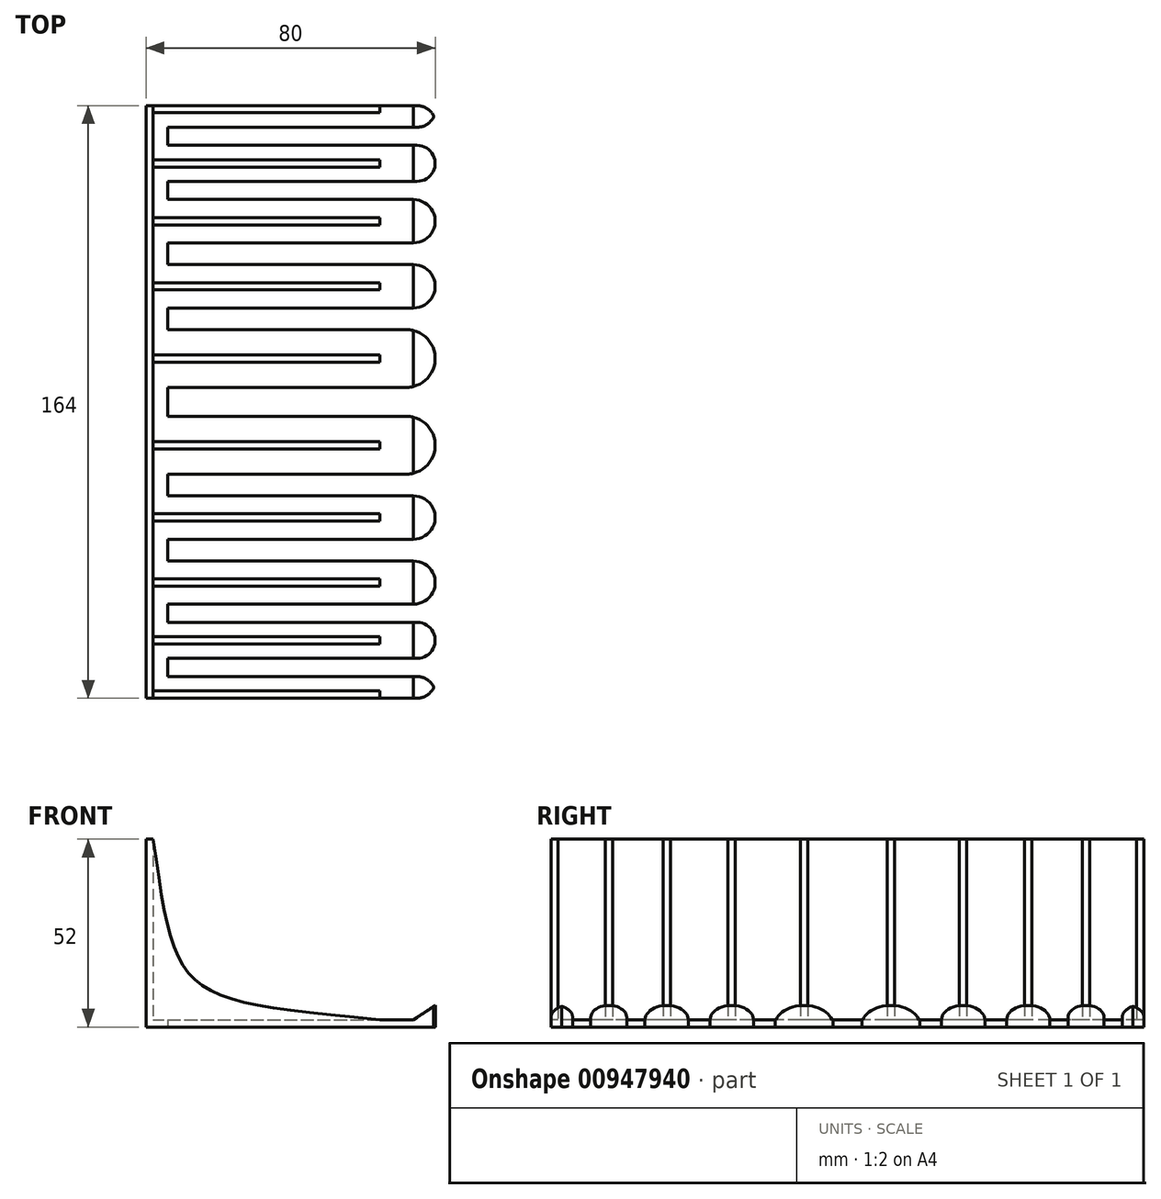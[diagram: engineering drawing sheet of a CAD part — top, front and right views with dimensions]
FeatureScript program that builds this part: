
annotation { "Feature Type Name" : "Feature", "Feature Type Description" : "" }
export const myFeature = defineFeature(function(context is Context, id is Id, definition is map)
    precondition{}
    {
        {
            assignVariable(context, id + "F0", {"name" : "thickness", "anyValue" : 2});
        }
        {
            assignVariable(context, id + "F1", {"name" : "height", "anyValue" : 50});
        }
        {
            var Q0;
            Q0=qCreatedBy(makeId("Top.planeOp"),FACE);
            var sketch = newSketch(context, id + "F2", { "sketchPlane" : qUnion([Q0])});
            skLineSegment(sketch, "E0", {"start": v(-21.89, -82.1) * mm, "end": v(47.11, -82.1) * mm});
            skLineSegment(sketch, "E1", {"start": v(52.11, -77.1) * mm, "end": v(52.11, -77.1) * mm});
            skLineSegment(sketch, "E2", {"start": v(47.11, -72.1) * mm, "end": v(-21.89, -72.1) * mm});
            skLineSegment(sketch, "E3", {"start": v(-21.89, -72.1) * mm, "end": v(-21.89, -67.1) * mm});
            skLineSegment(sketch, "E4", {"start": v(-21.89, -67.1) * mm, "end": v(46.11, -67.1) * mm});
            skLineSegment(sketch, "E5", {"start": v(52.11, -61.1) * mm, "end": v(52.11, -61.1) * mm});
            skLineSegment(sketch, "E6", {"start": v(46.11, -55.1) * mm, "end": v(-21.89, -55.1) * mm});
            skLineSegment(sketch, "E7", {"start": v(-21.89, -55.1) * mm, "end": v(-21.89, -49.1) * mm});
            skLineSegment(sketch, "E8", {"start": v(-21.89, -49.1) * mm, "end": v(46.11, -49.1) * mm});
            skLineSegment(sketch, "E9", {"start": v(52.11, -43.1) * mm, "end": v(52.11, -43.1) * mm});
            skLineSegment(sketch, "E10", {"start": v(46.11, -37.1) * mm, "end": v(-21.89, -37.1) * mm});
            skLineSegment(sketch, "E11", {"start": v(-21.89, -37.1) * mm, "end": v(-21.89, -31.1) * mm});
            skLineSegment(sketch, "E12", {"start": v(-21.89, -31.1) * mm, "end": v(44.11, -31.1) * mm});
            skLineSegment(sketch, "E13", {"start": v(52.11, -23.1) * mm, "end": v(52.11, -23.1) * mm});
            skLineSegment(sketch, "E14", {"start": v(44.11, -15.1) * mm, "end": v(-21.89, -15.1) * mm});
            skLineSegment(sketch, "E15", {"start": v(-21.89, -15.1) * mm, "end": v(-21.89, -7.1) * mm});
            skLineSegment(sketch, "E16", {"start": v(-21.89, -7.1) * mm, "end": v(44.11, -7.1) * mm});
            skLineSegment(sketch, "E17", {"start": v(52.11, 0.9) * mm, "end": v(52.11, 0.9) * mm});
            skLineSegment(sketch, "E18", {"start": v(44.11, 8.9) * mm, "end": v(-21.89, 8.9) * mm});
            skLineSegment(sketch, "E19", {"start": v(-21.89, 8.9) * mm, "end": v(-21.89, 14.9) * mm});
            skLineSegment(sketch, "E20", {"start": v(-21.89, 14.9) * mm, "end": v(46.11, 14.9) * mm});
            skLineSegment(sketch, "E21", {"start": v(52.11, 20.9) * mm, "end": v(52.11, 20.9) * mm});
            skLineSegment(sketch, "E22", {"start": v(46.11, 26.9) * mm, "end": v(-21.89, 26.9) * mm});
            skLineSegment(sketch, "E23", {"start": v(-21.89, 26.9) * mm, "end": v(-21.89, 32.9) * mm});
            skLineSegment(sketch, "E24", {"start": v(-21.89, 32.9) * mm, "end": v(46.11, 32.9) * mm});
            skLineSegment(sketch, "E25", {"start": v(52.11, 38.9) * mm, "end": v(52.11, 38.9) * mm});
            skLineSegment(sketch, "E26", {"start": v(46.11, 44.9) * mm, "end": v(-21.89, 44.9) * mm});
            skLineSegment(sketch, "E27", {"start": v(-21.89, 44.9) * mm, "end": v(-21.89, 49.9) * mm});
            skLineSegment(sketch, "E28", {"start": v(-21.89, 49.9) * mm, "end": v(47.11, 49.9) * mm});
            skLineSegment(sketch, "E29", {"start": v(52.11, 54.9) * mm, "end": v(52.11, 54.9) * mm});
            skLineSegment(sketch, "E30", {"start": v(47.11, 59.9) * mm, "end": v(-21.89, 59.9) * mm});
            skLineSegment(sketch, "E31", {"start": v(-21.89, -82.1) * mm, "end": v(-21.89, -87.1) * mm});
            skLineSegment(sketch, "E32", {"start": v(-21.89, -87.1) * mm, "end": v(47.11, -87.1) * mm});
            skLineSegment(sketch, "E33", {"start": v(52.11, -88.1) * mm, "end": v(52.11, -92.1) * mm});
            skLineSegment(sketch, "E34", {"start": v(47.11, -93.1) * mm, "end": v(-27.89, -93.1) * mm});
            skLineSegment(sketch, "E35", {"start": v(-21.89, 59.9) * mm, "end": v(-21.89, 64.9) * mm});
            skLineSegment(sketch, "E36", {"start": v(-21.89, 64.9) * mm, "end": v(47.11, 64.9) * mm});
            skLineSegment(sketch, "E37", {"start": v(52.11, 65.9) * mm, "end": v(52.11, 69.9) * mm});
            skLineSegment(sketch, "E38", {"start": v(47.11, 70.9) * mm, "end": v(-27.89, 70.9) * mm});
            skLineSegment(sketch, "E39", {"start": v(-27.89, 70.9) * mm, "end": v(-27.89, -93.1) * mm});
            skPoint(sketch, "E40.visualSharp", {"position": v(52.11, 70.9) * mm});
            skArc(sketch, "E40.filletArc", {"start": v(52.11, 65.9) * mm, "mid": v(50.65, 69.43) * mm, "end": v(47.11, 70.9) * mm});
            skPoint(sketch, "E41.visualSharp", {"position": v(52.11, 64.9) * mm});
            skArc(sketch, "E41.filletArc", {"start": v(47.11, 64.9) * mm, "mid": v(50.65, 66.36) * mm, "end": v(52.11, 69.9) * mm});
            skPoint(sketch, "E42.visualSharp", {"position": v(52.11, 59.9) * mm});
            skArc(sketch, "E42.filletArc", {"start": v(52.11, 54.9) * mm, "mid": v(50.65, 58.43) * mm, "end": v(47.11, 59.9) * mm});
            skPoint(sketch, "E43.visualSharp", {"position": v(52.11, 49.9) * mm});
            skArc(sketch, "E43.filletArc", {"start": v(47.11, 49.9) * mm, "mid": v(50.65, 51.36) * mm, "end": v(52.11, 54.9) * mm});
            skPoint(sketch, "E44.visualSharp", {"position": v(52.11, -87.1) * mm});
            skArc(sketch, "E44.filletArc", {"start": v(52.11, -92.1) * mm, "mid": v(50.65, -88.57) * mm, "end": v(47.11, -87.1) * mm});
            skPoint(sketch, "E45.visualSharp", {"position": v(52.11, -93.1) * mm});
            skArc(sketch, "E45.filletArc", {"start": v(47.11, -93.1) * mm, "mid": v(50.65, -91.64) * mm, "end": v(52.11, -88.1) * mm});
            skPoint(sketch, "E46.visualSharp", {"position": v(52.11, -82.1) * mm});
            skArc(sketch, "E46.filletArc", {"start": v(47.11, -82.1) * mm, "mid": v(50.65, -80.64) * mm, "end": v(52.11, -77.1) * mm});
            skPoint(sketch, "E47.visualSharp", {"position": v(52.11, -72.1) * mm});
            skArc(sketch, "E47.filletArc", {"start": v(52.11, -77.1) * mm, "mid": v(50.65, -73.57) * mm, "end": v(47.11, -72.1) * mm});
            skPoint(sketch, "E48.visualSharp", {"position": v(52.11, -67.1) * mm});
            skArc(sketch, "E48.filletArc", {"start": v(46.11, -67.1) * mm, "mid": v(50.35, -65.35) * mm, "end": v(52.11, -61.1) * mm});
            skPoint(sketch, "E49.visualSharp", {"position": v(52.11, -55.1) * mm});
            skArc(sketch, "E49.filletArc", {"start": v(52.11, -61.1) * mm, "mid": v(50.35, -56.86) * mm, "end": v(46.11, -55.1) * mm});
            skPoint(sketch, "E50.visualSharp", {"position": v(52.11, -49.1) * mm});
            skArc(sketch, "E50.filletArc", {"start": v(46.11, -49.1) * mm, "mid": v(50.35, -47.35) * mm, "end": v(52.11, -43.1) * mm});
            skPoint(sketch, "E51.visualSharp", {"position": v(52.11, -37.1) * mm});
            skArc(sketch, "E51.filletArc", {"start": v(52.11, -43.1) * mm, "mid": v(50.35, -38.86) * mm, "end": v(46.11, -37.1) * mm});
            skPoint(sketch, "E52.visualSharp", {"position": v(52.11, 44.9) * mm});
            skArc(sketch, "E52.filletArc", {"start": v(52.11, 38.9) * mm, "mid": v(50.35, 43.14) * mm, "end": v(46.11, 44.9) * mm});
            skPoint(sketch, "E53.visualSharp", {"position": v(52.11, 32.9) * mm});
            skArc(sketch, "E53.filletArc", {"start": v(46.11, 32.9) * mm, "mid": v(50.35, 34.65) * mm, "end": v(52.11, 38.9) * mm});
            skPoint(sketch, "E54.visualSharp", {"position": v(52.11, 26.9) * mm});
            skArc(sketch, "E54.filletArc", {"start": v(52.11, 20.9) * mm, "mid": v(50.35, 25.14) * mm, "end": v(46.11, 26.9) * mm});
            skPoint(sketch, "E55.visualSharp", {"position": v(52.11, 14.9) * mm});
            skArc(sketch, "E55.filletArc", {"start": v(46.11, 14.9) * mm, "mid": v(50.35, 16.65) * mm, "end": v(52.11, 20.9) * mm});
            skPoint(sketch, "E56.visualSharp", {"position": v(52.11, 8.9) * mm});
            skArc(sketch, "E56.filletArc", {"start": v(52.11, 0.9) * mm, "mid": v(49.77, 6.55) * mm, "end": v(44.11, 8.9) * mm});
            skPoint(sketch, "E57.visualSharp", {"position": v(52.11, -7.1) * mm});
            skArc(sketch, "E57.filletArc", {"start": v(44.11, -7.1) * mm, "mid": v(49.77, -4.76) * mm, "end": v(52.11, 0.9) * mm});
            skPoint(sketch, "E58.visualSharp", {"position": v(52.11, -15.1) * mm});
            skArc(sketch, "E58.filletArc", {"start": v(52.11, -23.1) * mm, "mid": v(49.77, -17.45) * mm, "end": v(44.11, -15.1) * mm});
            skPoint(sketch, "E59.visualSharp", {"position": v(52.11, -31.1) * mm});
            skArc(sketch, "E59.filletArc", {"start": v(44.11, -31.1) * mm, "mid": v(49.77, -28.76) * mm, "end": v(52.11, -23.1) * mm});
            skSolve(sketch);
        }
        {
            var Q0;
            Q0=makeQuery(id+"F2.imprint","IMPRINT",FACE,{"disambiguationData":[TD([[makeQuery(id+"F2.imprint","IMPRINT",EDGE,{"derivedFrom":sQuery(id+"F2.wireOp",EDGE,"E0")}),1.0]])]});
            extrude(context, id + "F3", {"entities" : qUnion([Q0]), "depth" : getVariable(context, 'thickness') * mm, "offsetDistance" : 25 * mm});
        }
        {
            var Q0;
            Q0=makeQuery(id+"F3.opExtrude","CAP_FACE",FACE,{"disambiguationData":[OSD([sQuery(id+"F2.wireOp",EDGE,"E0"),sQuery(id+"F2.wireOp",EDGE,"E2"),sQuery(id+"F2.wireOp",EDGE,"E3"),sQuery(id+"F2.wireOp",EDGE,"E4"),sQuery(id+"F2.wireOp",EDGE,"E6"),sQuery(id+"F2.wireOp",EDGE,"E7"),sQuery(id+"F2.wireOp",EDGE,"E8"),sQuery(id+"F2.wireOp",EDGE,"E10"),sQuery(id+"F2.wireOp",EDGE,"E11"),sQuery(id+"F2.wireOp",EDGE,"E12"),sQuery(id+"F2.wireOp",EDGE,"E14"),sQuery(id+"F2.wireOp",EDGE,"E15"),sQuery(id+"F2.wireOp",EDGE,"E16"),sQuery(id+"F2.wireOp",EDGE,"E18"),sQuery(id+"F2.wireOp",EDGE,"E19"),sQuery(id+"F2.wireOp",EDGE,"E20"),sQuery(id+"F2.wireOp",EDGE,"E22"),sQuery(id+"F2.wireOp",EDGE,"E23"),sQuery(id+"F2.wireOp",EDGE,"E24"),sQuery(id+"F2.wireOp",EDGE,"E26"),sQuery(id+"F2.wireOp",EDGE,"E27"),sQuery(id+"F2.wireOp",EDGE,"E28"),sQuery(id+"F2.wireOp",EDGE,"E30"),sQuery(id+"F2.wireOp",EDGE,"E31"),sQuery(id+"F2.wireOp",EDGE,"E32"),sQuery(id+"F2.wireOp",EDGE,"E34"),sQuery(id+"F2.wireOp",EDGE,"E35"),sQuery(id+"F2.wireOp",EDGE,"E36"),sQuery(id+"F2.wireOp",EDGE,"E38"),sQuery(id+"F2.wireOp",EDGE,"E39"),sQuery(id+"F2.wireOp",EDGE,"E40.filletArc"),sQuery(id+"F2.wireOp",EDGE,"E41.filletArc"),sQuery(id+"F2.wireOp",EDGE,"E42.filletArc"),sQuery(id+"F2.wireOp",EDGE,"E43.filletArc"),sQuery(id+"F2.wireOp",EDGE,"E44.filletArc"),sQuery(id+"F2.wireOp",EDGE,"E45.filletArc"),sQuery(id+"F2.wireOp",EDGE,"E46.filletArc"),sQuery(id+"F2.wireOp",EDGE,"E47.filletArc"),sQuery(id+"F2.wireOp",EDGE,"E48.filletArc"),sQuery(id+"F2.wireOp",EDGE,"E49.filletArc"),sQuery(id+"F2.wireOp",EDGE,"E50.filletArc"),sQuery(id+"F2.wireOp",EDGE,"E51.filletArc"),sQuery(id+"F2.wireOp",EDGE,"E52.filletArc"),sQuery(id+"F2.wireOp",EDGE,"E53.filletArc"),sQuery(id+"F2.wireOp",EDGE,"E54.filletArc"),sQuery(id+"F2.wireOp",EDGE,"E55.filletArc"),sQuery(id+"F2.wireOp",EDGE,"E56.filletArc"),sQuery(id+"F2.wireOp",EDGE,"E57.filletArc"),sQuery(id+"F2.wireOp",EDGE,"E58.filletArc"),sQuery(id+"F2.wireOp",EDGE,"E59.filletArc")])],"isStart":false});
            var sketch = newSketch(context, id + "F4", { "sketchPlane" : qUnion([Q0])});
            skLineSegment(sketch, "E60.bottom", {"start": v(-27.89, 70.9) * mm, "end": v(-25.89, 70.9) * mm});
            skLineSegment(sketch, "E60.top", {"start": v(-27.89, -93.1) * mm, "end": v(-25.89, -93.1) * mm});
            skLineSegment(sketch, "E60.left", {"start": v(-27.89, 70.9) * mm, "end": v(-27.89, -93.1) * mm});
            skLineSegment(sketch, "E60.right", {"start": v(-25.89, 70.9) * mm, "end": v(-25.89, -93.1) * mm});
            skSolve(sketch);
        }
        {
            var Q0;
            Q0=makeQuery(id+"F4.imprint","IMPRINT",FACE,{"disambiguationData":[TD([[makeQuery(id+"F4.imprint","IMPRINT",EDGE,{"derivedFrom":sQuery(id+"F4.wireOp",EDGE,"E60.bottom")}),1.0]])]});
            extrude(context, id + "F5", {"entities" : qUnion([Q0]), "operationType" : NewBodyOperationType.ADD, "depth" : getVariable(context, 'height') * mm, "offsetDistance" : 25 * mm});
        }
        {
            var Q0;
            Q0=makeQuery(id+"F5.boolean.opBoolean","MERGE",FACE,{"derivedFrom":[makeQuery(id+"F3.opExtrude","SWEPT_FACE",FACE,{"disambiguationData":[OSD([sQuery(id+"F2.wireOp",EDGE,"E34")])]}),makeQuery(id+"F5.opExtrude","SWEPT_FACE",FACE,{"disambiguationData":[OSD([sQuery(id+"F4.wireOp",EDGE,"E60.top")])]})]});
            var sketch = newSketch(context, id + "F6", { "sketchPlane" : qUnion([Q0])});
            skLineSegment(sketch, "E61", {"start": v(-25.89, 52) * mm, "end": v(-25.89, 2) * mm});
            skLineSegment(sketch, "E62", {"start": v(-25.89, 2) * mm, "end": v(36.73, 2) * mm});
            skFitSpline(sketch, "E63", {"points": [v(-25.89, 52) * mm, v(36.73, 2) * mm], "startDerivative": vector(18.74, -134.32) * mm, "endDerivative": vector(169.11, -16.45) * mm});
            skSolve(sketch);
        }
        {
            var Q0;
            Q0=makeQuery(id+"F6.imprint","IMPRINT",FACE,{"disambiguationData":[TD([[makeQuery(id+"F6.imprint","IMPRINT",EDGE,{"derivedFrom":sQuery(id+"F6.wireOp",EDGE,"E61")}),1.0]])]});
            var Q1;
            Q1=makeQuery(id+"F5.boolean.opBoolean","MERGE",FACE,{"derivedFrom":[makeQuery(id+"F3.opExtrude","SWEPT_FACE",FACE,{"disambiguationData":[OSD([sQuery(id+"F2.wireOp",EDGE,"E38")])]}),makeQuery(id+"F5.opExtrude","SWEPT_FACE",FACE,{"disambiguationData":[OSD([sQuery(id+"F4.wireOp",EDGE,"E60.bottom")])]})]});
            extrude(context, id + "F7", {"entities" : qUnion([Q0]), "operationType" : NewBodyOperationType.ADD, "endBound" : BoundingType.UP_TO_SURFACE, "oppositeDirection" : true, "depth" : 25 * mm, "endBoundEntityFace" : qUnion([Q1]), "offsetDistance" : 25 * mm});
        }
        {
            var Q0;
            {var subQ0=sQuery(id+"F2.wireOp",EDGE,"E49.filletArc");var subQ1=sQuery(id+"F2.wireOp",EDGE,"E48.filletArc");var subQ2=sQuery(id+"F2.wireOp",EDGE,"E6");var subQ3=sQuery(id+"F2.wireOp",EDGE,"E4");Q0=makeQuery(id+"F7.boolean.opBoolean","SPLIT",FACE,{"disambiguationData":[TD([makeQuery(id+"F3.opExtrude","SWEPT_FACE",FACE,{"disambiguationData":[OSD([subQ3])]})])],"derivedFrom":makeQuery(id+"F3.opExtrude","CAP_FACE",FACE,{"disambiguationData":[OSD([sQuery(id+"F2.wireOp",EDGE,"E0"),sQuery(id+"F2.wireOp",EDGE,"E2"),sQuery(id+"F2.wireOp",EDGE,"E3"),subQ3,subQ2,sQuery(id+"F2.wireOp",EDGE,"E7"),sQuery(id+"F2.wireOp",EDGE,"E8"),sQuery(id+"F2.wireOp",EDGE,"E10"),sQuery(id+"F2.wireOp",EDGE,"E11"),sQuery(id+"F2.wireOp",EDGE,"E12"),sQuery(id+"F2.wireOp",EDGE,"E14"),sQuery(id+"F2.wireOp",EDGE,"E15"),sQuery(id+"F2.wireOp",EDGE,"E16"),sQuery(id+"F2.wireOp",EDGE,"E18"),sQuery(id+"F2.wireOp",EDGE,"E19"),sQuery(id+"F2.wireOp",EDGE,"E20"),sQuery(id+"F2.wireOp",EDGE,"E22"),sQuery(id+"F2.wireOp",EDGE,"E23"),sQuery(id+"F2.wireOp",EDGE,"E24"),sQuery(id+"F2.wireOp",EDGE,"E26"),sQuery(id+"F2.wireOp",EDGE,"E27"),sQuery(id+"F2.wireOp",EDGE,"E28"),sQuery(id+"F2.wireOp",EDGE,"E30"),sQuery(id+"F2.wireOp",EDGE,"E31"),sQuery(id+"F2.wireOp",EDGE,"E32"),sQuery(id+"F2.wireOp",EDGE,"E34"),sQuery(id+"F2.wireOp",EDGE,"E35"),sQuery(id+"F2.wireOp",EDGE,"E36"),sQuery(id+"F2.wireOp",EDGE,"E38"),sQuery(id+"F2.wireOp",EDGE,"E39"),sQuery(id+"F2.wireOp",EDGE,"E40.filletArc"),sQuery(id+"F2.wireOp",EDGE,"E41.filletArc"),sQuery(id+"F2.wireOp",EDGE,"E42.filletArc"),sQuery(id+"F2.wireOp",EDGE,"E43.filletArc"),sQuery(id+"F2.wireOp",EDGE,"E44.filletArc"),sQuery(id+"F2.wireOp",EDGE,"E45.filletArc"),sQuery(id+"F2.wireOp",EDGE,"E46.filletArc"),sQuery(id+"F2.wireOp",EDGE,"E47.filletArc"),subQ1,subQ0,sQuery(id+"F2.wireOp",EDGE,"E50.filletArc"),sQuery(id+"F2.wireOp",EDGE,"E51.filletArc"),sQuery(id+"F2.wireOp",EDGE,"E52.filletArc"),sQuery(id+"F2.wireOp",EDGE,"E53.filletArc"),sQuery(id+"F2.wireOp",EDGE,"E54.filletArc"),sQuery(id+"F2.wireOp",EDGE,"E55.filletArc"),sQuery(id+"F2.wireOp",EDGE,"E56.filletArc"),sQuery(id+"F2.wireOp",EDGE,"E57.filletArc"),sQuery(id+"F2.wireOp",EDGE,"E58.filletArc"),sQuery(id+"F2.wireOp",EDGE,"E59.filletArc")])],"isStart":false})});}
            var sketch = newSketch(context, id + "F8", { "sketchPlane" : qUnion([Q0])});
            skPoint(sketch, "E64", {"position": v(36.73, -77.1) * mm});
            skPoint(sketch, "E65", {"position": v(36.73, -61.1) * mm});
            skPoint(sketch, "E66", {"position": v(36.73, -43.1) * mm});
            skPoint(sketch, "E67", {"position": v(36.73, -23.1) * mm});
            skPoint(sketch, "E68", {"position": v(36.73, 0.9) * mm});
            skPoint(sketch, "E69", {"position": v(36.73, 20.9) * mm});
            skPoint(sketch, "E70", {"position": v(36.73, 38.9) * mm});
            skPoint(sketch, "E71", {"position": v(36.73, 54.9) * mm});
            skLineSegment(sketch, "E72.bottom", {"start": v(36.73, -76.1) * mm, "end": v(-25.89, -76.1) * mm});
            skLineSegment(sketch, "E72.top", {"start": v(36.73, -78.1) * mm, "end": v(-25.89, -78.1) * mm});
            skLineSegment(sketch, "E72.left", {"start": v(36.73, -76.1) * mm, "end": v(36.73, -78.1) * mm});
            skLineSegment(sketch, "E72.right", {"start": v(-25.89, -76.1) * mm, "end": v(-25.89, -78.1) * mm});
            skLineSegment(sketch, "E73.bottom", {"start": v(36.73, -60.1) * mm, "end": v(-25.89, -60.1) * mm});
            skLineSegment(sketch, "E73.top", {"start": v(36.73, -62.1) * mm, "end": v(-25.89, -62.1) * mm});
            skLineSegment(sketch, "E73.left", {"start": v(36.73, -60.1) * mm, "end": v(36.73, -62.1) * mm});
            skLineSegment(sketch, "E73.right", {"start": v(-25.89, -60.1) * mm, "end": v(-25.89, -62.1) * mm});
            skLineSegment(sketch, "E74.bottom", {"start": v(36.73, -42.1) * mm, "end": v(-25.89, -42.1) * mm});
            skLineSegment(sketch, "E74.top", {"start": v(36.73, -44.1) * mm, "end": v(-25.89, -44.1) * mm});
            skLineSegment(sketch, "E74.left", {"start": v(36.73, -42.1) * mm, "end": v(36.73, -44.1) * mm});
            skLineSegment(sketch, "E74.right", {"start": v(-25.89, -42.1) * mm, "end": v(-25.89, -44.1) * mm});
            skLineSegment(sketch, "E75.bottom", {"start": v(36.73, -22.1) * mm, "end": v(-25.89, -22.1) * mm});
            skLineSegment(sketch, "E75.top", {"start": v(36.73, -24.1) * mm, "end": v(-25.89, -24.1) * mm});
            skLineSegment(sketch, "E75.left", {"start": v(36.73, -22.1) * mm, "end": v(36.73, -24.1) * mm});
            skLineSegment(sketch, "E75.right", {"start": v(-25.89, -22.1) * mm, "end": v(-25.89, -24.1) * mm});
            skLineSegment(sketch, "E76.bottom", {"start": v(36.73, 1.9) * mm, "end": v(-25.89, 1.9) * mm});
            skLineSegment(sketch, "E76.top", {"start": v(36.73, -0.1) * mm, "end": v(-25.89, -0.1) * mm});
            skLineSegment(sketch, "E76.left", {"start": v(36.73, 1.9) * mm, "end": v(36.73, -0.1) * mm});
            skLineSegment(sketch, "E76.right", {"start": v(-25.89, 1.9) * mm, "end": v(-25.89, -0.1) * mm});
            skLineSegment(sketch, "E77.bottom", {"start": v(36.73, 21.9) * mm, "end": v(-25.89, 21.9) * mm});
            skLineSegment(sketch, "E77.top", {"start": v(36.73, 19.9) * mm, "end": v(-25.89, 19.9) * mm});
            skLineSegment(sketch, "E77.left", {"start": v(36.73, 21.9) * mm, "end": v(36.73, 19.9) * mm});
            skLineSegment(sketch, "E77.right", {"start": v(-25.89, 21.9) * mm, "end": v(-25.89, 19.9) * mm});
            skLineSegment(sketch, "E78.bottom", {"start": v(36.73, 39.9) * mm, "end": v(-25.89, 39.9) * mm});
            skLineSegment(sketch, "E78.top", {"start": v(36.73, 37.9) * mm, "end": v(-25.89, 37.9) * mm});
            skLineSegment(sketch, "E78.left", {"start": v(36.73, 39.9) * mm, "end": v(36.73, 37.9) * mm});
            skLineSegment(sketch, "E78.right", {"start": v(-25.89, 39.9) * mm, "end": v(-25.89, 37.9) * mm});
            skLineSegment(sketch, "E79.bottom", {"start": v(36.73, 55.9) * mm, "end": v(-25.89, 55.9) * mm});
            skLineSegment(sketch, "E79.top", {"start": v(36.73, 53.9) * mm, "end": v(-25.89, 53.9) * mm});
            skLineSegment(sketch, "E79.left", {"start": v(36.73, 55.9) * mm, "end": v(36.73, 53.9) * mm});
            skLineSegment(sketch, "E79.right", {"start": v(-25.89, 55.9) * mm, "end": v(-25.89, 53.9) * mm});
            skPoint(sketch, "E80", {"position": v(-25.89, 68.9) * mm});
            skPoint(sketch, "E81", {"position": v(36.73, -91.1) * mm});
            skLineSegment(sketch, "E82.bottom", {"start": v(-25.89, 68.9) * mm, "end": v(36.73, 68.9) * mm});
            skLineSegment(sketch, "E82.top", {"start": v(-25.89, -91.1) * mm, "end": v(36.73, -91.1) * mm});
            skLineSegment(sketch, "E82.left", {"start": v(-25.89, 68.9) * mm, "end": v(-25.89, -91.1) * mm});
            skLineSegment(sketch, "E82.right", {"start": v(36.73, 68.9) * mm, "end": v(36.73, -91.1) * mm});
            skSolve(sketch);
        }
        {
            var Q0;
            {var subQ1=sQuery(id+"F8.wireOp",EDGE,"E72.top");Q0=makeQuery(id+"F8.imprint","IMPRINT",FACE,{"disambiguationData":[TD([[makeQuery(id+"F8.imprint","IMPRINT",EDGE,{"derivedFrom":subQ1}),1.0]])]});}
            var Q1;
            {var subQ1=sQuery(id+"F8.wireOp",EDGE,"E72.bottom");Q1=makeQuery(id+"F8.imprint","IMPRINT",FACE,{"disambiguationData":[TD([[makeQuery(id+"F8.imprint","IMPRINT",EDGE,{"derivedFrom":subQ1}),-1.0]])]});}
            var Q2;
            {var subQ5=sQuery(id+"F8.wireOp",EDGE,"E73.bottom");Q2=makeQuery(id+"F8.imprint","IMPRINT",FACE,{"disambiguationData":[TD([[makeQuery(id+"F8.imprint","IMPRINT",EDGE,{"derivedFrom":subQ5}),-1.0]])]});}
            var Q3;
            {var subQ5=sQuery(id+"F8.wireOp",EDGE,"E74.bottom");Q3=makeQuery(id+"F8.imprint","IMPRINT",FACE,{"disambiguationData":[TD([[makeQuery(id+"F8.imprint","IMPRINT",EDGE,{"derivedFrom":subQ5}),-1.0]])]});}
            var Q4;
            {var subQ2=sQuery(id+"F8.wireOp",EDGE,"E75.bottom");Q4=makeQuery(id+"F8.imprint","IMPRINT",FACE,{"disambiguationData":[TD([[makeQuery(id+"F8.imprint","IMPRINT",EDGE,{"derivedFrom":subQ2}),-1.0]])]});}
            var Q5;
            {var subQ5=sQuery(id+"F8.wireOp",EDGE,"E76.bottom");Q5=makeQuery(id+"F8.imprint","IMPRINT",FACE,{"disambiguationData":[TD([[makeQuery(id+"F8.imprint","IMPRINT",EDGE,{"derivedFrom":subQ5}),-1.0]])]});}
            var Q6;
            {var subQ1=sQuery(id+"F8.wireOp",EDGE,"E77.bottom");Q6=makeQuery(id+"F8.imprint","IMPRINT",FACE,{"disambiguationData":[TD([[makeQuery(id+"F8.imprint","IMPRINT",EDGE,{"derivedFrom":subQ1}),-1.0]])]});}
            var Q7;
            {var subQ5=sQuery(id+"F8.wireOp",EDGE,"E78.bottom");Q7=makeQuery(id+"F8.imprint","IMPRINT",FACE,{"disambiguationData":[TD([[makeQuery(id+"F8.imprint","IMPRINT",EDGE,{"derivedFrom":subQ5}),-1.0]])]});}
            var Q8;
            {var subQ5=sQuery(id+"F8.wireOp",EDGE,"E79.bottom");Q8=makeQuery(id+"F8.imprint","IMPRINT",FACE,{"disambiguationData":[TD([[makeQuery(id+"F8.imprint","IMPRINT",EDGE,{"derivedFrom":subQ5}),-1.0]])]});}
            var Q9;
            Q9=makeQuery(id+"F5.opExtrude","CAP_FACE",FACE,{"disambiguationData":[OSD([sQuery(id+"F4.wireOp",EDGE,"E60.bottom"),sQuery(id+"F4.wireOp",EDGE,"E60.top"),sQuery(id+"F4.wireOp",EDGE,"E60.left"),sQuery(id+"F4.wireOp",EDGE,"E60.right")])],"isStart":false});
            extrude(context, id + "F9", {"entities" : qUnion([Q0, Q1, Q2, Q3, Q4, Q5, Q6, Q7, Q8]), "operationType" : NewBodyOperationType.REMOVE, "endBound" : BoundingType.UP_TO_SURFACE, "depth" : 25 * mm, "endBoundEntityFace" : qUnion([Q9]), "offsetDistance" : 25 * mm});
        }
        {
            var Q0;
            {var subQ0=sQuery(id+"F8.wireOp",EDGE,"E82.right");var subQ1=sQuery(id+"F8.wireOp",EDGE,"E82.left");var subQ4=sQuery(id+"F2.wireOp",EDGE,"E14");var subQ5=sQuery(id+"F2.wireOp",EDGE,"E59.filletArc");var subQ6=sQuery(id+"F2.wireOp",EDGE,"E58.filletArc");var subQ7=sQuery(id+"F2.wireOp",EDGE,"E12");var subQ10=sQuery(id+"F2.wireOp",EDGE,"E57.filletArc");var subQ11=sQuery(id+"F2.wireOp",EDGE,"E56.filletArc");var subQ12=sQuery(id+"F2.wireOp",EDGE,"E55.filletArc");var subQ13=sQuery(id+"F2.wireOp",EDGE,"E54.filletArc");var subQ14=sQuery(id+"F2.wireOp",EDGE,"E53.filletArc");var subQ15=sQuery(id+"F2.wireOp",EDGE,"E52.filletArc");var subQ16=sQuery(id+"F2.wireOp",EDGE,"E51.filletArc");var subQ17=sQuery(id+"F2.wireOp",EDGE,"E50.filletArc");var subQ18=sQuery(id+"F2.wireOp",EDGE,"E49.filletArc");var subQ19=sQuery(id+"F2.wireOp",EDGE,"E48.filletArc");var subQ20=sQuery(id+"F2.wireOp",EDGE,"E47.filletArc");var subQ21=sQuery(id+"F2.wireOp",EDGE,"E46.filletArc");var subQ22=sQuery(id+"F2.wireOp",EDGE,"E45.filletArc");var subQ23=sQuery(id+"F2.wireOp",EDGE,"E44.filletArc");var subQ24=sQuery(id+"F2.wireOp",EDGE,"E43.filletArc");var subQ25=sQuery(id+"F2.wireOp",EDGE,"E42.filletArc");var subQ26=sQuery(id+"F2.wireOp",EDGE,"E41.filletArc");var subQ27=sQuery(id+"F2.wireOp",EDGE,"E40.filletArc");var subQ28=sQuery(id+"F2.wireOp",EDGE,"E38");var subQ29=sQuery(id+"F2.wireOp",EDGE,"E36");var subQ30=sQuery(id+"F2.wireOp",EDGE,"E34");var subQ31=sQuery(id+"F2.wireOp",EDGE,"E32");var subQ32=sQuery(id+"F2.wireOp",EDGE,"E30");var subQ33=sQuery(id+"F2.wireOp",EDGE,"E28");var subQ34=sQuery(id+"F2.wireOp",EDGE,"E26");var subQ35=sQuery(id+"F2.wireOp",EDGE,"E24");var subQ36=sQuery(id+"F2.wireOp",EDGE,"E22");var subQ37=sQuery(id+"F2.wireOp",EDGE,"E20");var subQ38=sQuery(id+"F2.wireOp",EDGE,"E18");var subQ39=sQuery(id+"F2.wireOp",EDGE,"E16");var subQ40=sQuery(id+"F2.wireOp",EDGE,"E10");var subQ41=sQuery(id+"F2.wireOp",EDGE,"E8");var subQ42=sQuery(id+"F2.wireOp",EDGE,"E6");var subQ43=sQuery(id+"F2.wireOp",EDGE,"E4");var subQ44=sQuery(id+"F2.wireOp",EDGE,"E2");var subQ45=sQuery(id+"F2.wireOp",EDGE,"E0");var subQ46=makeQuery(id+"F3.opExtrude","CAP_FACE",FACE,{"disambiguationData":[OSD([subQ45,subQ44,sQuery(id+"F2.wireOp",EDGE,"E3"),subQ43,subQ42,sQuery(id+"F2.wireOp",EDGE,"E7"),subQ41,subQ40,sQuery(id+"F2.wireOp",EDGE,"E11"),subQ7,subQ4,sQuery(id+"F2.wireOp",EDGE,"E15"),subQ39,subQ38,sQuery(id+"F2.wireOp",EDGE,"E19"),subQ37,subQ36,sQuery(id+"F2.wireOp",EDGE,"E23"),subQ35,subQ34,sQuery(id+"F2.wireOp",EDGE,"E27"),subQ33,subQ32,sQuery(id+"F2.wireOp",EDGE,"E31"),subQ31,subQ30,sQuery(id+"F2.wireOp",EDGE,"E35"),subQ29,subQ28,sQuery(id+"F2.wireOp",EDGE,"E39"),subQ27,subQ26,subQ25,subQ24,subQ23,subQ22,subQ21,subQ20,subQ19,subQ18,subQ17,subQ16,subQ15,subQ14,subQ13,subQ12,subQ11,subQ10,subQ6,subQ5])],"isStart":false});Q0=makeQuery(id+"F9.boolean.opBoolean","MERGE",FACE,{"derivedFrom":[makeQuery(id+"F7.boolean.opBoolean","SPLIT",FACE,{"disambiguationData":[TD([makeQuery(id+"F3.opExtrude","SWEPT_FACE",FACE,{"disambiguationData":[OSD([subQ29])]})])],"derivedFrom":subQ46}),makeQuery(id+"F7.boolean.opBoolean","SPLIT",FACE,{"disambiguationData":[TD([makeQuery(id+"F3.opExtrude","SWEPT_FACE",FACE,{"disambiguationData":[OSD([subQ31])]})])],"derivedFrom":subQ46}),makeQuery(id+"F7.boolean.opBoolean","SPLIT",FACE,{"disambiguationData":[TD([makeQuery(id+"F3.opExtrude","SWEPT_FACE",FACE,{"disambiguationData":[OSD([subQ33])]})])],"derivedFrom":subQ46}),makeQuery(id+"F7.boolean.opBoolean","SPLIT",FACE,{"disambiguationData":[TD([makeQuery(id+"F3.opExtrude","SWEPT_FACE",FACE,{"disambiguationData":[OSD([subQ45])]})])],"derivedFrom":subQ46}),makeQuery(id+"F7.boolean.opBoolean","SPLIT",FACE,{"disambiguationData":[TD([makeQuery(id+"F3.opExtrude","SWEPT_FACE",FACE,{"disambiguationData":[OSD([subQ43])]})])],"derivedFrom":subQ46}),makeQuery(id+"F7.boolean.opBoolean","SPLIT",FACE,{"disambiguationData":[TD([makeQuery(id+"F3.opExtrude","SWEPT_FACE",FACE,{"disambiguationData":[OSD([subQ41])]})])],"derivedFrom":subQ46}),makeQuery(id+"F7.boolean.opBoolean","SPLIT",FACE,{"disambiguationData":[TD([makeQuery(id+"F3.opExtrude","SWEPT_FACE",FACE,{"disambiguationData":[OSD([subQ35])]})])],"derivedFrom":subQ46}),makeQuery(id+"F7.boolean.opBoolean","SPLIT",FACE,{"disambiguationData":[TD([makeQuery(id+"F3.opExtrude","SWEPT_FACE",FACE,{"disambiguationData":[OSD([subQ37])]})])],"derivedFrom":subQ46}),makeQuery(id+"F7.boolean.opBoolean","SPLIT",FACE,{"disambiguationData":[TD([makeQuery(id+"F3.opExtrude","SWEPT_FACE",FACE,{"disambiguationData":[OSD([subQ39])]})])],"derivedFrom":subQ46}),makeQuery(id+"F7.boolean.opBoolean","SPLIT",FACE,{"disambiguationData":[TD([makeQuery(id+"F3.opExtrude","SWEPT_FACE",FACE,{"disambiguationData":[OSD([subQ7])]})])],"derivedFrom":subQ46})],"fromTools":[makeQuery(id+"F9.opExtrude","CAP_FACE",FACE,{"disambiguationData":[OSD([sQuery(id+"F8.wireOp",EDGE,"E72.bottom"),sQuery(id+"F8.wireOp",EDGE,"E73.top"),subQ1,subQ0])],"isStart":true}),makeQuery(id+"F9.opExtrude","CAP_FACE",FACE,{"disambiguationData":[OSD([sQuery(id+"F8.wireOp",EDGE,"E72.top"),sQuery(id+"F8.wireOp",EDGE,"E82.top"),subQ1,subQ0])],"isStart":true}),makeQuery(id+"F9.opExtrude","CAP_FACE",FACE,{"disambiguationData":[OSD([sQuery(id+"F8.wireOp",EDGE,"E73.bottom"),sQuery(id+"F8.wireOp",EDGE,"E74.top"),subQ1,subQ0])],"isStart":true}),makeQuery(id+"F9.opExtrude","CAP_FACE",FACE,{"disambiguationData":[OSD([sQuery(id+"F8.wireOp",EDGE,"E74.bottom"),sQuery(id+"F8.wireOp",EDGE,"E75.top"),subQ1,subQ0])],"isStart":true}),makeQuery(id+"F9.opExtrude","CAP_FACE",FACE,{"disambiguationData":[OSD([sQuery(id+"F8.wireOp",EDGE,"E75.bottom"),sQuery(id+"F8.wireOp",EDGE,"E76.top"),subQ1,subQ0])],"isStart":true}),makeQuery(id+"F9.opExtrude","CAP_FACE",FACE,{"disambiguationData":[OSD([sQuery(id+"F8.wireOp",EDGE,"E76.bottom"),sQuery(id+"F8.wireOp",EDGE,"E77.top"),subQ1,subQ0])],"isStart":true}),makeQuery(id+"F9.opExtrude","CAP_FACE",FACE,{"disambiguationData":[OSD([sQuery(id+"F8.wireOp",EDGE,"E77.bottom"),sQuery(id+"F8.wireOp",EDGE,"E78.top"),subQ1,subQ0])],"isStart":true}),makeQuery(id+"F9.opExtrude","CAP_FACE",FACE,{"disambiguationData":[OSD([sQuery(id+"F8.wireOp",EDGE,"E78.bottom"),sQuery(id+"F8.wireOp",EDGE,"E79.top"),subQ1,subQ0])],"isStart":true}),makeQuery(id+"F9.opExtrude","CAP_FACE",FACE,{"disambiguationData":[OSD([sQuery(id+"F8.wireOp",EDGE,"E79.bottom"),sQuery(id+"F8.wireOp",EDGE,"E82.bottom"),subQ1,subQ0])],"isStart":true})]});}
            var sketch = newSketch(context, id + "F10", { "sketchPlane" : qUnion([Q0])});
            skLineSegment(sketch, "E83", {"start": v(46.11, 70.9) * mm, "end": v(46.11, -93.1) * mm});
            skSolve(sketch);
        }
        {
            var Q0;
            {var subQ7=sQuery(id+"F2.wireOp",EDGE,"E45.filletArc");var subQ8=sQuery(id+"F2.wireOp",EDGE,"E44.filletArc");var subQ11=makeQuery(id+"F3.opExtrude","CAP_EDGE",EDGE,{"disambiguationData":[OSD([subQ8,subQ7])],"isStart":false});Q0=makeQuery(id+"F10.imprint","IMPRINT",FACE,{"disambiguationData":[TD([[makeQuery(id+"F10.imprint","IMPRINT",EDGE,{"derivedFrom":subQ11}),1.0]])]});}
            var Q1;
            {var subQ5=sQuery(id+"F2.wireOp",EDGE,"E47.filletArc");var subQ6=sQuery(id+"F2.wireOp",EDGE,"E46.filletArc");var subQ15=makeQuery(id+"F3.opExtrude","CAP_EDGE",EDGE,{"disambiguationData":[OSD([subQ6,subQ5])],"isStart":false});Q1=makeQuery(id+"F10.imprint","IMPRINT",FACE,{"disambiguationData":[TD([[makeQuery(id+"F10.imprint","IMPRINT",EDGE,{"derivedFrom":subQ15}),1.0]])]});}
            var Q2;
            {var subQ5=sQuery(id+"F2.wireOp",EDGE,"E49.filletArc");var subQ6=sQuery(id+"F2.wireOp",EDGE,"E48.filletArc");var subQ15=makeQuery(id+"F3.opExtrude","CAP_EDGE",EDGE,{"disambiguationData":[OSD([subQ6,subQ5])],"isStart":false});Q2=makeQuery(id+"F10.imprint","IMPRINT",FACE,{"disambiguationData":[TD([[makeQuery(id+"F10.imprint","IMPRINT",EDGE,{"derivedFrom":subQ15}),1.0]])]});}
            var Q3;
            {var subQ5=sQuery(id+"F2.wireOp",EDGE,"E51.filletArc");var subQ6=sQuery(id+"F2.wireOp",EDGE,"E50.filletArc");var subQ15=makeQuery(id+"F3.opExtrude","CAP_EDGE",EDGE,{"disambiguationData":[OSD([subQ6,subQ5])],"isStart":false});Q3=makeQuery(id+"F10.imprint","IMPRINT",FACE,{"disambiguationData":[TD([[makeQuery(id+"F10.imprint","IMPRINT",EDGE,{"derivedFrom":subQ15}),1.0]])]});}
            var Q4;
            {var subQ5=sQuery(id+"F2.wireOp",EDGE,"E59.filletArc");var subQ6=sQuery(id+"F2.wireOp",EDGE,"E58.filletArc");var subQ15=makeQuery(id+"F3.opExtrude","CAP_EDGE",EDGE,{"disambiguationData":[OSD([subQ6,subQ5])],"isStart":false});Q4=makeQuery(id+"F10.imprint","IMPRINT",FACE,{"disambiguationData":[TD([[makeQuery(id+"F10.imprint","IMPRINT",EDGE,{"derivedFrom":subQ15}),1.0]])]});}
            var Q5;
            {var subQ5=sQuery(id+"F2.wireOp",EDGE,"E57.filletArc");var subQ6=sQuery(id+"F2.wireOp",EDGE,"E56.filletArc");var subQ15=makeQuery(id+"F3.opExtrude","CAP_EDGE",EDGE,{"disambiguationData":[OSD([subQ6,subQ5])],"isStart":false});Q5=makeQuery(id+"F10.imprint","IMPRINT",FACE,{"disambiguationData":[TD([[makeQuery(id+"F10.imprint","IMPRINT",EDGE,{"derivedFrom":subQ15}),1.0]])]});}
            var Q6;
            {var subQ5=sQuery(id+"F2.wireOp",EDGE,"E55.filletArc");var subQ6=sQuery(id+"F2.wireOp",EDGE,"E54.filletArc");var subQ15=makeQuery(id+"F3.opExtrude","CAP_EDGE",EDGE,{"disambiguationData":[OSD([subQ6,subQ5])],"isStart":false});Q6=makeQuery(id+"F10.imprint","IMPRINT",FACE,{"disambiguationData":[TD([[makeQuery(id+"F10.imprint","IMPRINT",EDGE,{"derivedFrom":subQ15}),1.0]])]});}
            var Q7;
            {var subQ5=sQuery(id+"F2.wireOp",EDGE,"E53.filletArc");var subQ6=sQuery(id+"F2.wireOp",EDGE,"E52.filletArc");var subQ15=makeQuery(id+"F3.opExtrude","CAP_EDGE",EDGE,{"disambiguationData":[OSD([subQ6,subQ5])],"isStart":false});Q7=makeQuery(id+"F10.imprint","IMPRINT",FACE,{"disambiguationData":[TD([[makeQuery(id+"F10.imprint","IMPRINT",EDGE,{"derivedFrom":subQ15}),1.0]])]});}
            var Q8;
            {var subQ5=sQuery(id+"F2.wireOp",EDGE,"E43.filletArc");var subQ6=sQuery(id+"F2.wireOp",EDGE,"E42.filletArc");var subQ15=makeQuery(id+"F3.opExtrude","CAP_EDGE",EDGE,{"disambiguationData":[OSD([subQ6,subQ5])],"isStart":false});Q8=makeQuery(id+"F10.imprint","IMPRINT",FACE,{"disambiguationData":[TD([[makeQuery(id+"F10.imprint","IMPRINT",EDGE,{"derivedFrom":subQ15}),1.0]])]});}
            var Q9;
            {var subQ7=sQuery(id+"F2.wireOp",EDGE,"E41.filletArc");var subQ8=sQuery(id+"F2.wireOp",EDGE,"E40.filletArc");var subQ11=makeQuery(id+"F3.opExtrude","CAP_EDGE",EDGE,{"disambiguationData":[OSD([subQ8,subQ7])],"isStart":false});Q9=makeQuery(id+"F10.imprint","IMPRINT",FACE,{"disambiguationData":[TD([[makeQuery(id+"F10.imprint","IMPRINT",EDGE,{"derivedFrom":subQ11}),1.0]])]});}
            extrude(context, id + "F11", {"entities" : qUnion([Q0, Q1, Q2, Q3, Q4, Q5, Q6, Q7, Q8, Q9]), "operationType" : NewBodyOperationType.ADD, "depth" : 4 * mm, "offsetDistance" : 25 * mm});
        }
        {
            var Q0;
            {var subQ0=sQuery(id+"F10.wireOp",EDGE,"E83");var subQ1=sQuery(id+"F2.wireOp",EDGE,"E34");Q0=makeQuery(id+"F11.opExtrude","CAP_EDGE",EDGE,{"disambiguationData":[OSD([subQ0]),TDD([makeQuery(id+"F10.imprint","IMPRINT",EDGE,{"disambiguationData":[TD([[makeQuery(id+"F10.imprint","INTERSECT",VERTEX,{"derivedFrom":[makeQuery(id+"F3.opExtrude","CAP_EDGE",EDGE,{"disambiguationData":[OSD([subQ1])],"isStart":false}),subQ0]}),1.0]])],"derivedFrom":subQ0})])],"isStart":false});}
            var Q1;
            {var subQ0=sQuery(id+"F10.wireOp",EDGE,"E83");var subQ1=sQuery(id+"F2.wireOp",EDGE,"E2");var subQ3=makeQuery(id+"F7.opExtrude","SWEPT_FACE",FACE,{"disambiguationData":[OSD([sQuery(id+"F6.wireOp",EDGE,"E62")])]});var subQ4=makeQuery(id+"F3.opExtrude","CAP_EDGE",EDGE,{"disambiguationData":[OSD([subQ1])],"isStart":false});var subQ5=sQuery(id+"F2.wireOp",EDGE,"E0");var subQ6=makeQuery(id+"F3.opExtrude","CAP_FACE",FACE,{"disambiguationData":[OSD([subQ5,subQ1,sQuery(id+"F2.wireOp",EDGE,"E3"),sQuery(id+"F2.wireOp",EDGE,"E4"),sQuery(id+"F2.wireOp",EDGE,"E6"),sQuery(id+"F2.wireOp",EDGE,"E7"),sQuery(id+"F2.wireOp",EDGE,"E8"),sQuery(id+"F2.wireOp",EDGE,"E10"),sQuery(id+"F2.wireOp",EDGE,"E11"),sQuery(id+"F2.wireOp",EDGE,"E12"),sQuery(id+"F2.wireOp",EDGE,"E14"),sQuery(id+"F2.wireOp",EDGE,"E15"),sQuery(id+"F2.wireOp",EDGE,"E16"),sQuery(id+"F2.wireOp",EDGE,"E18"),sQuery(id+"F2.wireOp",EDGE,"E19"),sQuery(id+"F2.wireOp",EDGE,"E20"),sQuery(id+"F2.wireOp",EDGE,"E22"),sQuery(id+"F2.wireOp",EDGE,"E23"),sQuery(id+"F2.wireOp",EDGE,"E24"),sQuery(id+"F2.wireOp",EDGE,"E26"),sQuery(id+"F2.wireOp",EDGE,"E27"),sQuery(id+"F2.wireOp",EDGE,"E28"),sQuery(id+"F2.wireOp",EDGE,"E30"),sQuery(id+"F2.wireOp",EDGE,"E31"),sQuery(id+"F2.wireOp",EDGE,"E32"),sQuery(id+"F2.wireOp",EDGE,"E34"),sQuery(id+"F2.wireOp",EDGE,"E35"),sQuery(id+"F2.wireOp",EDGE,"E36"),sQuery(id+"F2.wireOp",EDGE,"E38"),sQuery(id+"F2.wireOp",EDGE,"E39"),sQuery(id+"F2.wireOp",EDGE,"E40.filletArc"),sQuery(id+"F2.wireOp",EDGE,"E41.filletArc"),sQuery(id+"F2.wireOp",EDGE,"E42.filletArc"),sQuery(id+"F2.wireOp",EDGE,"E43.filletArc"),sQuery(id+"F2.wireOp",EDGE,"E44.filletArc"),sQuery(id+"F2.wireOp",EDGE,"E45.filletArc"),sQuery(id+"F2.wireOp",EDGE,"E46.filletArc"),sQuery(id+"F2.wireOp",EDGE,"E47.filletArc"),sQuery(id+"F2.wireOp",EDGE,"E48.filletArc"),sQuery(id+"F2.wireOp",EDGE,"E49.filletArc"),sQuery(id+"F2.wireOp",EDGE,"E50.filletArc"),sQuery(id+"F2.wireOp",EDGE,"E51.filletArc"),sQuery(id+"F2.wireOp",EDGE,"E52.filletArc"),sQuery(id+"F2.wireOp",EDGE,"E53.filletArc"),sQuery(id+"F2.wireOp",EDGE,"E54.filletArc"),sQuery(id+"F2.wireOp",EDGE,"E55.filletArc"),sQuery(id+"F2.wireOp",EDGE,"E56.filletArc"),sQuery(id+"F2.wireOp",EDGE,"E57.filletArc"),sQuery(id+"F2.wireOp",EDGE,"E58.filletArc"),sQuery(id+"F2.wireOp",EDGE,"E59.filletArc")])],"isStart":false});Q1=makeQuery(id+"F11.opExtrude","CAP_EDGE",EDGE,{"disambiguationData":[OSD([subQ0]),TDD([makeQuery(id+"F10.imprint","IMPRINT",EDGE,{"disambiguationData":[TD([[makeQuery(id+"F10.imprint","INTERSECT",VERTEX,{"derivedFrom":[makeQuery(id+"F9.boolean.opBoolean","MERGE",EDGE,{"derivedFrom":[makeQuery(id+"F7.boolean.opBoolean","SPLIT",EDGE,{"disambiguationData":[topologyDisambiguationEdgeConnected([subQ6])],"derivedFrom":subQ4}),makeQuery(id+"F7.boolean.opBoolean","SPLIT",EDGE,{"disambiguationData":[topologyDisambiguationEdgeConnected([subQ3])],"derivedFrom":subQ4})]}),subQ0]}),-1.0]])],"derivedFrom":subQ0})])],"isStart":false});}
            var Q2;
            {var subQ0=sQuery(id+"F10.wireOp",EDGE,"E83");var subQ1=sQuery(id+"F2.wireOp",EDGE,"E6");var subQ3=makeQuery(id+"F7.opExtrude","SWEPT_FACE",FACE,{"disambiguationData":[OSD([sQuery(id+"F6.wireOp",EDGE,"E62")])]});var subQ4=makeQuery(id+"F3.opExtrude","CAP_EDGE",EDGE,{"disambiguationData":[OSD([subQ1])],"isStart":false});var subQ5=sQuery(id+"F2.wireOp",EDGE,"E4");var subQ6=makeQuery(id+"F3.opExtrude","CAP_FACE",FACE,{"disambiguationData":[OSD([sQuery(id+"F2.wireOp",EDGE,"E0"),sQuery(id+"F2.wireOp",EDGE,"E2"),sQuery(id+"F2.wireOp",EDGE,"E3"),subQ5,subQ1,sQuery(id+"F2.wireOp",EDGE,"E7"),sQuery(id+"F2.wireOp",EDGE,"E8"),sQuery(id+"F2.wireOp",EDGE,"E10"),sQuery(id+"F2.wireOp",EDGE,"E11"),sQuery(id+"F2.wireOp",EDGE,"E12"),sQuery(id+"F2.wireOp",EDGE,"E14"),sQuery(id+"F2.wireOp",EDGE,"E15"),sQuery(id+"F2.wireOp",EDGE,"E16"),sQuery(id+"F2.wireOp",EDGE,"E18"),sQuery(id+"F2.wireOp",EDGE,"E19"),sQuery(id+"F2.wireOp",EDGE,"E20"),sQuery(id+"F2.wireOp",EDGE,"E22"),sQuery(id+"F2.wireOp",EDGE,"E23"),sQuery(id+"F2.wireOp",EDGE,"E24"),sQuery(id+"F2.wireOp",EDGE,"E26"),sQuery(id+"F2.wireOp",EDGE,"E27"),sQuery(id+"F2.wireOp",EDGE,"E28"),sQuery(id+"F2.wireOp",EDGE,"E30"),sQuery(id+"F2.wireOp",EDGE,"E31"),sQuery(id+"F2.wireOp",EDGE,"E32"),sQuery(id+"F2.wireOp",EDGE,"E34"),sQuery(id+"F2.wireOp",EDGE,"E35"),sQuery(id+"F2.wireOp",EDGE,"E36"),sQuery(id+"F2.wireOp",EDGE,"E38"),sQuery(id+"F2.wireOp",EDGE,"E39"),sQuery(id+"F2.wireOp",EDGE,"E40.filletArc"),sQuery(id+"F2.wireOp",EDGE,"E41.filletArc"),sQuery(id+"F2.wireOp",EDGE,"E42.filletArc"),sQuery(id+"F2.wireOp",EDGE,"E43.filletArc"),sQuery(id+"F2.wireOp",EDGE,"E44.filletArc"),sQuery(id+"F2.wireOp",EDGE,"E45.filletArc"),sQuery(id+"F2.wireOp",EDGE,"E46.filletArc"),sQuery(id+"F2.wireOp",EDGE,"E47.filletArc"),sQuery(id+"F2.wireOp",EDGE,"E48.filletArc"),sQuery(id+"F2.wireOp",EDGE,"E49.filletArc"),sQuery(id+"F2.wireOp",EDGE,"E50.filletArc"),sQuery(id+"F2.wireOp",EDGE,"E51.filletArc"),sQuery(id+"F2.wireOp",EDGE,"E52.filletArc"),sQuery(id+"F2.wireOp",EDGE,"E53.filletArc"),sQuery(id+"F2.wireOp",EDGE,"E54.filletArc"),sQuery(id+"F2.wireOp",EDGE,"E55.filletArc"),sQuery(id+"F2.wireOp",EDGE,"E56.filletArc"),sQuery(id+"F2.wireOp",EDGE,"E57.filletArc"),sQuery(id+"F2.wireOp",EDGE,"E58.filletArc"),sQuery(id+"F2.wireOp",EDGE,"E59.filletArc")])],"isStart":false});Q2=makeQuery(id+"F11.opExtrude","CAP_EDGE",EDGE,{"disambiguationData":[OSD([subQ0]),TDD([makeQuery(id+"F10.imprint","IMPRINT",EDGE,{"disambiguationData":[TD([[makeQuery(id+"F10.imprint","INTERSECT",VERTEX,{"derivedFrom":[makeQuery(id+"F9.boolean.opBoolean","MERGE",EDGE,{"derivedFrom":[makeQuery(id+"F7.boolean.opBoolean","SPLIT",EDGE,{"disambiguationData":[topologyDisambiguationEdgeConnected([subQ6])],"derivedFrom":subQ4}),makeQuery(id+"F7.boolean.opBoolean","SPLIT",EDGE,{"disambiguationData":[topologyDisambiguationEdgeConnected([subQ3])],"derivedFrom":subQ4})]}),subQ0]}),-1.0]])],"derivedFrom":subQ0})])],"isStart":false});}
            var Q3;
            {var subQ0=sQuery(id+"F10.wireOp",EDGE,"E83");var subQ1=sQuery(id+"F2.wireOp",EDGE,"E10");var subQ3=makeQuery(id+"F7.opExtrude","SWEPT_FACE",FACE,{"disambiguationData":[OSD([sQuery(id+"F6.wireOp",EDGE,"E62")])]});var subQ4=makeQuery(id+"F3.opExtrude","CAP_EDGE",EDGE,{"disambiguationData":[OSD([subQ1])],"isStart":false});var subQ5=sQuery(id+"F2.wireOp",EDGE,"E8");var subQ6=makeQuery(id+"F3.opExtrude","CAP_FACE",FACE,{"disambiguationData":[OSD([sQuery(id+"F2.wireOp",EDGE,"E0"),sQuery(id+"F2.wireOp",EDGE,"E2"),sQuery(id+"F2.wireOp",EDGE,"E3"),sQuery(id+"F2.wireOp",EDGE,"E4"),sQuery(id+"F2.wireOp",EDGE,"E6"),sQuery(id+"F2.wireOp",EDGE,"E7"),subQ5,subQ1,sQuery(id+"F2.wireOp",EDGE,"E11"),sQuery(id+"F2.wireOp",EDGE,"E12"),sQuery(id+"F2.wireOp",EDGE,"E14"),sQuery(id+"F2.wireOp",EDGE,"E15"),sQuery(id+"F2.wireOp",EDGE,"E16"),sQuery(id+"F2.wireOp",EDGE,"E18"),sQuery(id+"F2.wireOp",EDGE,"E19"),sQuery(id+"F2.wireOp",EDGE,"E20"),sQuery(id+"F2.wireOp",EDGE,"E22"),sQuery(id+"F2.wireOp",EDGE,"E23"),sQuery(id+"F2.wireOp",EDGE,"E24"),sQuery(id+"F2.wireOp",EDGE,"E26"),sQuery(id+"F2.wireOp",EDGE,"E27"),sQuery(id+"F2.wireOp",EDGE,"E28"),sQuery(id+"F2.wireOp",EDGE,"E30"),sQuery(id+"F2.wireOp",EDGE,"E31"),sQuery(id+"F2.wireOp",EDGE,"E32"),sQuery(id+"F2.wireOp",EDGE,"E34"),sQuery(id+"F2.wireOp",EDGE,"E35"),sQuery(id+"F2.wireOp",EDGE,"E36"),sQuery(id+"F2.wireOp",EDGE,"E38"),sQuery(id+"F2.wireOp",EDGE,"E39"),sQuery(id+"F2.wireOp",EDGE,"E40.filletArc"),sQuery(id+"F2.wireOp",EDGE,"E41.filletArc"),sQuery(id+"F2.wireOp",EDGE,"E42.filletArc"),sQuery(id+"F2.wireOp",EDGE,"E43.filletArc"),sQuery(id+"F2.wireOp",EDGE,"E44.filletArc"),sQuery(id+"F2.wireOp",EDGE,"E45.filletArc"),sQuery(id+"F2.wireOp",EDGE,"E46.filletArc"),sQuery(id+"F2.wireOp",EDGE,"E47.filletArc"),sQuery(id+"F2.wireOp",EDGE,"E48.filletArc"),sQuery(id+"F2.wireOp",EDGE,"E49.filletArc"),sQuery(id+"F2.wireOp",EDGE,"E50.filletArc"),sQuery(id+"F2.wireOp",EDGE,"E51.filletArc"),sQuery(id+"F2.wireOp",EDGE,"E52.filletArc"),sQuery(id+"F2.wireOp",EDGE,"E53.filletArc"),sQuery(id+"F2.wireOp",EDGE,"E54.filletArc"),sQuery(id+"F2.wireOp",EDGE,"E55.filletArc"),sQuery(id+"F2.wireOp",EDGE,"E56.filletArc"),sQuery(id+"F2.wireOp",EDGE,"E57.filletArc"),sQuery(id+"F2.wireOp",EDGE,"E58.filletArc"),sQuery(id+"F2.wireOp",EDGE,"E59.filletArc")])],"isStart":false});Q3=makeQuery(id+"F11.opExtrude","CAP_EDGE",EDGE,{"disambiguationData":[OSD([subQ0]),TDD([makeQuery(id+"F10.imprint","IMPRINT",EDGE,{"disambiguationData":[TD([[makeQuery(id+"F10.imprint","INTERSECT",VERTEX,{"derivedFrom":[makeQuery(id+"F9.boolean.opBoolean","MERGE",EDGE,{"derivedFrom":[makeQuery(id+"F7.boolean.opBoolean","SPLIT",EDGE,{"disambiguationData":[topologyDisambiguationEdgeConnected([subQ6])],"derivedFrom":subQ4}),makeQuery(id+"F7.boolean.opBoolean","SPLIT",EDGE,{"disambiguationData":[topologyDisambiguationEdgeConnected([subQ3])],"derivedFrom":subQ4})]}),subQ0]}),-1.0]])],"derivedFrom":subQ0})])],"isStart":false});}
            var Q4;
            {var subQ0=sQuery(id+"F10.wireOp",EDGE,"E83");var subQ1=sQuery(id+"F2.wireOp",EDGE,"E14");var subQ3=makeQuery(id+"F7.opExtrude","SWEPT_FACE",FACE,{"disambiguationData":[OSD([sQuery(id+"F6.wireOp",EDGE,"E62")])]});var subQ4=makeQuery(id+"F3.opExtrude","CAP_EDGE",EDGE,{"disambiguationData":[OSD([subQ1])],"isStart":false});var subQ5=sQuery(id+"F2.wireOp",EDGE,"E12");var subQ6=makeQuery(id+"F3.opExtrude","CAP_FACE",FACE,{"disambiguationData":[OSD([sQuery(id+"F2.wireOp",EDGE,"E0"),sQuery(id+"F2.wireOp",EDGE,"E2"),sQuery(id+"F2.wireOp",EDGE,"E3"),sQuery(id+"F2.wireOp",EDGE,"E4"),sQuery(id+"F2.wireOp",EDGE,"E6"),sQuery(id+"F2.wireOp",EDGE,"E7"),sQuery(id+"F2.wireOp",EDGE,"E8"),sQuery(id+"F2.wireOp",EDGE,"E10"),sQuery(id+"F2.wireOp",EDGE,"E11"),subQ5,subQ1,sQuery(id+"F2.wireOp",EDGE,"E15"),sQuery(id+"F2.wireOp",EDGE,"E16"),sQuery(id+"F2.wireOp",EDGE,"E18"),sQuery(id+"F2.wireOp",EDGE,"E19"),sQuery(id+"F2.wireOp",EDGE,"E20"),sQuery(id+"F2.wireOp",EDGE,"E22"),sQuery(id+"F2.wireOp",EDGE,"E23"),sQuery(id+"F2.wireOp",EDGE,"E24"),sQuery(id+"F2.wireOp",EDGE,"E26"),sQuery(id+"F2.wireOp",EDGE,"E27"),sQuery(id+"F2.wireOp",EDGE,"E28"),sQuery(id+"F2.wireOp",EDGE,"E30"),sQuery(id+"F2.wireOp",EDGE,"E31"),sQuery(id+"F2.wireOp",EDGE,"E32"),sQuery(id+"F2.wireOp",EDGE,"E34"),sQuery(id+"F2.wireOp",EDGE,"E35"),sQuery(id+"F2.wireOp",EDGE,"E36"),sQuery(id+"F2.wireOp",EDGE,"E38"),sQuery(id+"F2.wireOp",EDGE,"E39"),sQuery(id+"F2.wireOp",EDGE,"E40.filletArc"),sQuery(id+"F2.wireOp",EDGE,"E41.filletArc"),sQuery(id+"F2.wireOp",EDGE,"E42.filletArc"),sQuery(id+"F2.wireOp",EDGE,"E43.filletArc"),sQuery(id+"F2.wireOp",EDGE,"E44.filletArc"),sQuery(id+"F2.wireOp",EDGE,"E45.filletArc"),sQuery(id+"F2.wireOp",EDGE,"E46.filletArc"),sQuery(id+"F2.wireOp",EDGE,"E47.filletArc"),sQuery(id+"F2.wireOp",EDGE,"E48.filletArc"),sQuery(id+"F2.wireOp",EDGE,"E49.filletArc"),sQuery(id+"F2.wireOp",EDGE,"E50.filletArc"),sQuery(id+"F2.wireOp",EDGE,"E51.filletArc"),sQuery(id+"F2.wireOp",EDGE,"E52.filletArc"),sQuery(id+"F2.wireOp",EDGE,"E53.filletArc"),sQuery(id+"F2.wireOp",EDGE,"E54.filletArc"),sQuery(id+"F2.wireOp",EDGE,"E55.filletArc"),sQuery(id+"F2.wireOp",EDGE,"E56.filletArc"),sQuery(id+"F2.wireOp",EDGE,"E57.filletArc"),sQuery(id+"F2.wireOp",EDGE,"E58.filletArc"),sQuery(id+"F2.wireOp",EDGE,"E59.filletArc")])],"isStart":false});Q4=makeQuery(id+"F11.opExtrude","CAP_EDGE",EDGE,{"disambiguationData":[OSD([subQ0]),TDD([makeQuery(id+"F10.imprint","IMPRINT",EDGE,{"disambiguationData":[TD([[makeQuery(id+"F10.imprint","INTERSECT",VERTEX,{"derivedFrom":[makeQuery(id+"F9.boolean.opBoolean","MERGE",EDGE,{"derivedFrom":[makeQuery(id+"F7.boolean.opBoolean","SPLIT",EDGE,{"disambiguationData":[topologyDisambiguationEdgeConnected([subQ6])],"derivedFrom":subQ4}),makeQuery(id+"F7.boolean.opBoolean","SPLIT",EDGE,{"disambiguationData":[topologyDisambiguationEdgeConnected([subQ3])],"derivedFrom":subQ4})]}),subQ0]}),-1.0]])],"derivedFrom":subQ0})])],"isStart":false});}
            var Q5;
            {var subQ0=sQuery(id+"F10.wireOp",EDGE,"E83");var subQ1=sQuery(id+"F2.wireOp",EDGE,"E18");var subQ3=makeQuery(id+"F7.opExtrude","SWEPT_FACE",FACE,{"disambiguationData":[OSD([sQuery(id+"F6.wireOp",EDGE,"E62")])]});var subQ4=makeQuery(id+"F3.opExtrude","CAP_EDGE",EDGE,{"disambiguationData":[OSD([subQ1])],"isStart":false});var subQ5=sQuery(id+"F2.wireOp",EDGE,"E16");var subQ6=makeQuery(id+"F3.opExtrude","CAP_FACE",FACE,{"disambiguationData":[OSD([sQuery(id+"F2.wireOp",EDGE,"E0"),sQuery(id+"F2.wireOp",EDGE,"E2"),sQuery(id+"F2.wireOp",EDGE,"E3"),sQuery(id+"F2.wireOp",EDGE,"E4"),sQuery(id+"F2.wireOp",EDGE,"E6"),sQuery(id+"F2.wireOp",EDGE,"E7"),sQuery(id+"F2.wireOp",EDGE,"E8"),sQuery(id+"F2.wireOp",EDGE,"E10"),sQuery(id+"F2.wireOp",EDGE,"E11"),sQuery(id+"F2.wireOp",EDGE,"E12"),sQuery(id+"F2.wireOp",EDGE,"E14"),sQuery(id+"F2.wireOp",EDGE,"E15"),subQ5,subQ1,sQuery(id+"F2.wireOp",EDGE,"E19"),sQuery(id+"F2.wireOp",EDGE,"E20"),sQuery(id+"F2.wireOp",EDGE,"E22"),sQuery(id+"F2.wireOp",EDGE,"E23"),sQuery(id+"F2.wireOp",EDGE,"E24"),sQuery(id+"F2.wireOp",EDGE,"E26"),sQuery(id+"F2.wireOp",EDGE,"E27"),sQuery(id+"F2.wireOp",EDGE,"E28"),sQuery(id+"F2.wireOp",EDGE,"E30"),sQuery(id+"F2.wireOp",EDGE,"E31"),sQuery(id+"F2.wireOp",EDGE,"E32"),sQuery(id+"F2.wireOp",EDGE,"E34"),sQuery(id+"F2.wireOp",EDGE,"E35"),sQuery(id+"F2.wireOp",EDGE,"E36"),sQuery(id+"F2.wireOp",EDGE,"E38"),sQuery(id+"F2.wireOp",EDGE,"E39"),sQuery(id+"F2.wireOp",EDGE,"E40.filletArc"),sQuery(id+"F2.wireOp",EDGE,"E41.filletArc"),sQuery(id+"F2.wireOp",EDGE,"E42.filletArc"),sQuery(id+"F2.wireOp",EDGE,"E43.filletArc"),sQuery(id+"F2.wireOp",EDGE,"E44.filletArc"),sQuery(id+"F2.wireOp",EDGE,"E45.filletArc"),sQuery(id+"F2.wireOp",EDGE,"E46.filletArc"),sQuery(id+"F2.wireOp",EDGE,"E47.filletArc"),sQuery(id+"F2.wireOp",EDGE,"E48.filletArc"),sQuery(id+"F2.wireOp",EDGE,"E49.filletArc"),sQuery(id+"F2.wireOp",EDGE,"E50.filletArc"),sQuery(id+"F2.wireOp",EDGE,"E51.filletArc"),sQuery(id+"F2.wireOp",EDGE,"E52.filletArc"),sQuery(id+"F2.wireOp",EDGE,"E53.filletArc"),sQuery(id+"F2.wireOp",EDGE,"E54.filletArc"),sQuery(id+"F2.wireOp",EDGE,"E55.filletArc"),sQuery(id+"F2.wireOp",EDGE,"E56.filletArc"),sQuery(id+"F2.wireOp",EDGE,"E57.filletArc"),sQuery(id+"F2.wireOp",EDGE,"E58.filletArc"),sQuery(id+"F2.wireOp",EDGE,"E59.filletArc")])],"isStart":false});Q5=makeQuery(id+"F11.opExtrude","CAP_EDGE",EDGE,{"disambiguationData":[OSD([subQ0]),TDD([makeQuery(id+"F10.imprint","IMPRINT",EDGE,{"disambiguationData":[TD([[makeQuery(id+"F10.imprint","INTERSECT",VERTEX,{"derivedFrom":[makeQuery(id+"F9.boolean.opBoolean","MERGE",EDGE,{"derivedFrom":[makeQuery(id+"F7.boolean.opBoolean","SPLIT",EDGE,{"disambiguationData":[topologyDisambiguationEdgeConnected([subQ6])],"derivedFrom":subQ4}),makeQuery(id+"F7.boolean.opBoolean","SPLIT",EDGE,{"disambiguationData":[topologyDisambiguationEdgeConnected([subQ3])],"derivedFrom":subQ4})]}),subQ0]}),-1.0]])],"derivedFrom":subQ0})])],"isStart":false});}
            var Q6;
            {var subQ0=sQuery(id+"F10.wireOp",EDGE,"E83");var subQ1=sQuery(id+"F2.wireOp",EDGE,"E22");var subQ3=makeQuery(id+"F7.opExtrude","SWEPT_FACE",FACE,{"disambiguationData":[OSD([sQuery(id+"F6.wireOp",EDGE,"E62")])]});var subQ4=makeQuery(id+"F3.opExtrude","CAP_EDGE",EDGE,{"disambiguationData":[OSD([subQ1])],"isStart":false});var subQ5=sQuery(id+"F2.wireOp",EDGE,"E20");var subQ6=makeQuery(id+"F3.opExtrude","CAP_FACE",FACE,{"disambiguationData":[OSD([sQuery(id+"F2.wireOp",EDGE,"E0"),sQuery(id+"F2.wireOp",EDGE,"E2"),sQuery(id+"F2.wireOp",EDGE,"E3"),sQuery(id+"F2.wireOp",EDGE,"E4"),sQuery(id+"F2.wireOp",EDGE,"E6"),sQuery(id+"F2.wireOp",EDGE,"E7"),sQuery(id+"F2.wireOp",EDGE,"E8"),sQuery(id+"F2.wireOp",EDGE,"E10"),sQuery(id+"F2.wireOp",EDGE,"E11"),sQuery(id+"F2.wireOp",EDGE,"E12"),sQuery(id+"F2.wireOp",EDGE,"E14"),sQuery(id+"F2.wireOp",EDGE,"E15"),sQuery(id+"F2.wireOp",EDGE,"E16"),sQuery(id+"F2.wireOp",EDGE,"E18"),sQuery(id+"F2.wireOp",EDGE,"E19"),subQ5,subQ1,sQuery(id+"F2.wireOp",EDGE,"E23"),sQuery(id+"F2.wireOp",EDGE,"E24"),sQuery(id+"F2.wireOp",EDGE,"E26"),sQuery(id+"F2.wireOp",EDGE,"E27"),sQuery(id+"F2.wireOp",EDGE,"E28"),sQuery(id+"F2.wireOp",EDGE,"E30"),sQuery(id+"F2.wireOp",EDGE,"E31"),sQuery(id+"F2.wireOp",EDGE,"E32"),sQuery(id+"F2.wireOp",EDGE,"E34"),sQuery(id+"F2.wireOp",EDGE,"E35"),sQuery(id+"F2.wireOp",EDGE,"E36"),sQuery(id+"F2.wireOp",EDGE,"E38"),sQuery(id+"F2.wireOp",EDGE,"E39"),sQuery(id+"F2.wireOp",EDGE,"E40.filletArc"),sQuery(id+"F2.wireOp",EDGE,"E41.filletArc"),sQuery(id+"F2.wireOp",EDGE,"E42.filletArc"),sQuery(id+"F2.wireOp",EDGE,"E43.filletArc"),sQuery(id+"F2.wireOp",EDGE,"E44.filletArc"),sQuery(id+"F2.wireOp",EDGE,"E45.filletArc"),sQuery(id+"F2.wireOp",EDGE,"E46.filletArc"),sQuery(id+"F2.wireOp",EDGE,"E47.filletArc"),sQuery(id+"F2.wireOp",EDGE,"E48.filletArc"),sQuery(id+"F2.wireOp",EDGE,"E49.filletArc"),sQuery(id+"F2.wireOp",EDGE,"E50.filletArc"),sQuery(id+"F2.wireOp",EDGE,"E51.filletArc"),sQuery(id+"F2.wireOp",EDGE,"E52.filletArc"),sQuery(id+"F2.wireOp",EDGE,"E53.filletArc"),sQuery(id+"F2.wireOp",EDGE,"E54.filletArc"),sQuery(id+"F2.wireOp",EDGE,"E55.filletArc"),sQuery(id+"F2.wireOp",EDGE,"E56.filletArc"),sQuery(id+"F2.wireOp",EDGE,"E57.filletArc"),sQuery(id+"F2.wireOp",EDGE,"E58.filletArc"),sQuery(id+"F2.wireOp",EDGE,"E59.filletArc")])],"isStart":false});Q6=makeQuery(id+"F11.opExtrude","CAP_EDGE",EDGE,{"disambiguationData":[OSD([subQ0]),TDD([makeQuery(id+"F10.imprint","IMPRINT",EDGE,{"disambiguationData":[TD([[makeQuery(id+"F10.imprint","INTERSECT",VERTEX,{"derivedFrom":[makeQuery(id+"F9.boolean.opBoolean","MERGE",EDGE,{"derivedFrom":[makeQuery(id+"F7.boolean.opBoolean","SPLIT",EDGE,{"disambiguationData":[topologyDisambiguationEdgeConnected([subQ6])],"derivedFrom":subQ4}),makeQuery(id+"F7.boolean.opBoolean","SPLIT",EDGE,{"disambiguationData":[topologyDisambiguationEdgeConnected([subQ3])],"derivedFrom":subQ4})]}),subQ0]}),-1.0]])],"derivedFrom":subQ0})])],"isStart":false});}
            var Q7;
            {var subQ0=sQuery(id+"F10.wireOp",EDGE,"E83");var subQ1=sQuery(id+"F2.wireOp",EDGE,"E26");var subQ3=makeQuery(id+"F7.opExtrude","SWEPT_FACE",FACE,{"disambiguationData":[OSD([sQuery(id+"F6.wireOp",EDGE,"E62")])]});var subQ4=makeQuery(id+"F3.opExtrude","CAP_EDGE",EDGE,{"disambiguationData":[OSD([subQ1])],"isStart":false});var subQ5=sQuery(id+"F2.wireOp",EDGE,"E24");var subQ6=makeQuery(id+"F3.opExtrude","CAP_FACE",FACE,{"disambiguationData":[OSD([sQuery(id+"F2.wireOp",EDGE,"E0"),sQuery(id+"F2.wireOp",EDGE,"E2"),sQuery(id+"F2.wireOp",EDGE,"E3"),sQuery(id+"F2.wireOp",EDGE,"E4"),sQuery(id+"F2.wireOp",EDGE,"E6"),sQuery(id+"F2.wireOp",EDGE,"E7"),sQuery(id+"F2.wireOp",EDGE,"E8"),sQuery(id+"F2.wireOp",EDGE,"E10"),sQuery(id+"F2.wireOp",EDGE,"E11"),sQuery(id+"F2.wireOp",EDGE,"E12"),sQuery(id+"F2.wireOp",EDGE,"E14"),sQuery(id+"F2.wireOp",EDGE,"E15"),sQuery(id+"F2.wireOp",EDGE,"E16"),sQuery(id+"F2.wireOp",EDGE,"E18"),sQuery(id+"F2.wireOp",EDGE,"E19"),sQuery(id+"F2.wireOp",EDGE,"E20"),sQuery(id+"F2.wireOp",EDGE,"E22"),sQuery(id+"F2.wireOp",EDGE,"E23"),subQ5,subQ1,sQuery(id+"F2.wireOp",EDGE,"E27"),sQuery(id+"F2.wireOp",EDGE,"E28"),sQuery(id+"F2.wireOp",EDGE,"E30"),sQuery(id+"F2.wireOp",EDGE,"E31"),sQuery(id+"F2.wireOp",EDGE,"E32"),sQuery(id+"F2.wireOp",EDGE,"E34"),sQuery(id+"F2.wireOp",EDGE,"E35"),sQuery(id+"F2.wireOp",EDGE,"E36"),sQuery(id+"F2.wireOp",EDGE,"E38"),sQuery(id+"F2.wireOp",EDGE,"E39"),sQuery(id+"F2.wireOp",EDGE,"E40.filletArc"),sQuery(id+"F2.wireOp",EDGE,"E41.filletArc"),sQuery(id+"F2.wireOp",EDGE,"E42.filletArc"),sQuery(id+"F2.wireOp",EDGE,"E43.filletArc"),sQuery(id+"F2.wireOp",EDGE,"E44.filletArc"),sQuery(id+"F2.wireOp",EDGE,"E45.filletArc"),sQuery(id+"F2.wireOp",EDGE,"E46.filletArc"),sQuery(id+"F2.wireOp",EDGE,"E47.filletArc"),sQuery(id+"F2.wireOp",EDGE,"E48.filletArc"),sQuery(id+"F2.wireOp",EDGE,"E49.filletArc"),sQuery(id+"F2.wireOp",EDGE,"E50.filletArc"),sQuery(id+"F2.wireOp",EDGE,"E51.filletArc"),sQuery(id+"F2.wireOp",EDGE,"E52.filletArc"),sQuery(id+"F2.wireOp",EDGE,"E53.filletArc"),sQuery(id+"F2.wireOp",EDGE,"E54.filletArc"),sQuery(id+"F2.wireOp",EDGE,"E55.filletArc"),sQuery(id+"F2.wireOp",EDGE,"E56.filletArc"),sQuery(id+"F2.wireOp",EDGE,"E57.filletArc"),sQuery(id+"F2.wireOp",EDGE,"E58.filletArc"),sQuery(id+"F2.wireOp",EDGE,"E59.filletArc")])],"isStart":false});Q7=makeQuery(id+"F11.opExtrude","CAP_EDGE",EDGE,{"disambiguationData":[OSD([subQ0]),TDD([makeQuery(id+"F10.imprint","IMPRINT",EDGE,{"disambiguationData":[TD([[makeQuery(id+"F10.imprint","INTERSECT",VERTEX,{"derivedFrom":[makeQuery(id+"F9.boolean.opBoolean","MERGE",EDGE,{"derivedFrom":[makeQuery(id+"F7.boolean.opBoolean","SPLIT",EDGE,{"disambiguationData":[topologyDisambiguationEdgeConnected([subQ6])],"derivedFrom":subQ4}),makeQuery(id+"F7.boolean.opBoolean","SPLIT",EDGE,{"disambiguationData":[topologyDisambiguationEdgeConnected([subQ3])],"derivedFrom":subQ4})]}),subQ0]}),-1.0]])],"derivedFrom":subQ0})])],"isStart":false});}
            var Q8;
            {var subQ0=sQuery(id+"F10.wireOp",EDGE,"E83");var subQ1=sQuery(id+"F2.wireOp",EDGE,"E30");var subQ3=makeQuery(id+"F7.opExtrude","SWEPT_FACE",FACE,{"disambiguationData":[OSD([sQuery(id+"F6.wireOp",EDGE,"E62")])]});var subQ4=makeQuery(id+"F3.opExtrude","CAP_EDGE",EDGE,{"disambiguationData":[OSD([subQ1])],"isStart":false});var subQ5=sQuery(id+"F2.wireOp",EDGE,"E28");var subQ6=makeQuery(id+"F3.opExtrude","CAP_FACE",FACE,{"disambiguationData":[OSD([sQuery(id+"F2.wireOp",EDGE,"E0"),sQuery(id+"F2.wireOp",EDGE,"E2"),sQuery(id+"F2.wireOp",EDGE,"E3"),sQuery(id+"F2.wireOp",EDGE,"E4"),sQuery(id+"F2.wireOp",EDGE,"E6"),sQuery(id+"F2.wireOp",EDGE,"E7"),sQuery(id+"F2.wireOp",EDGE,"E8"),sQuery(id+"F2.wireOp",EDGE,"E10"),sQuery(id+"F2.wireOp",EDGE,"E11"),sQuery(id+"F2.wireOp",EDGE,"E12"),sQuery(id+"F2.wireOp",EDGE,"E14"),sQuery(id+"F2.wireOp",EDGE,"E15"),sQuery(id+"F2.wireOp",EDGE,"E16"),sQuery(id+"F2.wireOp",EDGE,"E18"),sQuery(id+"F2.wireOp",EDGE,"E19"),sQuery(id+"F2.wireOp",EDGE,"E20"),sQuery(id+"F2.wireOp",EDGE,"E22"),sQuery(id+"F2.wireOp",EDGE,"E23"),sQuery(id+"F2.wireOp",EDGE,"E24"),sQuery(id+"F2.wireOp",EDGE,"E26"),sQuery(id+"F2.wireOp",EDGE,"E27"),subQ5,subQ1,sQuery(id+"F2.wireOp",EDGE,"E31"),sQuery(id+"F2.wireOp",EDGE,"E32"),sQuery(id+"F2.wireOp",EDGE,"E34"),sQuery(id+"F2.wireOp",EDGE,"E35"),sQuery(id+"F2.wireOp",EDGE,"E36"),sQuery(id+"F2.wireOp",EDGE,"E38"),sQuery(id+"F2.wireOp",EDGE,"E39"),sQuery(id+"F2.wireOp",EDGE,"E40.filletArc"),sQuery(id+"F2.wireOp",EDGE,"E41.filletArc"),sQuery(id+"F2.wireOp",EDGE,"E42.filletArc"),sQuery(id+"F2.wireOp",EDGE,"E43.filletArc"),sQuery(id+"F2.wireOp",EDGE,"E44.filletArc"),sQuery(id+"F2.wireOp",EDGE,"E45.filletArc"),sQuery(id+"F2.wireOp",EDGE,"E46.filletArc"),sQuery(id+"F2.wireOp",EDGE,"E47.filletArc"),sQuery(id+"F2.wireOp",EDGE,"E48.filletArc"),sQuery(id+"F2.wireOp",EDGE,"E49.filletArc"),sQuery(id+"F2.wireOp",EDGE,"E50.filletArc"),sQuery(id+"F2.wireOp",EDGE,"E51.filletArc"),sQuery(id+"F2.wireOp",EDGE,"E52.filletArc"),sQuery(id+"F2.wireOp",EDGE,"E53.filletArc"),sQuery(id+"F2.wireOp",EDGE,"E54.filletArc"),sQuery(id+"F2.wireOp",EDGE,"E55.filletArc"),sQuery(id+"F2.wireOp",EDGE,"E56.filletArc"),sQuery(id+"F2.wireOp",EDGE,"E57.filletArc"),sQuery(id+"F2.wireOp",EDGE,"E58.filletArc"),sQuery(id+"F2.wireOp",EDGE,"E59.filletArc")])],"isStart":false});Q8=makeQuery(id+"F11.opExtrude","CAP_EDGE",EDGE,{"disambiguationData":[OSD([subQ0]),TDD([makeQuery(id+"F10.imprint","IMPRINT",EDGE,{"disambiguationData":[TD([[makeQuery(id+"F10.imprint","INTERSECT",VERTEX,{"derivedFrom":[makeQuery(id+"F9.boolean.opBoolean","MERGE",EDGE,{"derivedFrom":[makeQuery(id+"F7.boolean.opBoolean","SPLIT",EDGE,{"disambiguationData":[topologyDisambiguationEdgeConnected([subQ6])],"derivedFrom":subQ4}),makeQuery(id+"F7.boolean.opBoolean","SPLIT",EDGE,{"disambiguationData":[topologyDisambiguationEdgeConnected([subQ3])],"derivedFrom":subQ4})]}),subQ0]}),-1.0]])],"derivedFrom":subQ0})])],"isStart":false});}
            var Q9;
            {var subQ0=sQuery(id+"F10.wireOp",EDGE,"E83");var subQ1=sQuery(id+"F2.wireOp",EDGE,"E38");Q9=makeQuery(id+"F11.opExtrude","CAP_EDGE",EDGE,{"disambiguationData":[OSD([subQ0]),TDD([makeQuery(id+"F10.imprint","IMPRINT",EDGE,{"disambiguationData":[TD([[makeQuery(id+"F10.imprint","INTERSECT",VERTEX,{"derivedFrom":[makeQuery(id+"F3.opExtrude","CAP_EDGE",EDGE,{"disambiguationData":[OSD([subQ1])],"isStart":false}),subQ0]}),-1.0]])],"derivedFrom":subQ0})])],"isStart":false});}
            chamfer(context, id + "F12", {"entities" : qUnion([Q0, Q1, Q2, Q3, Q4, Q5, Q6, Q7, Q8, Q9]), "chamferType" : ChamferType.TWO_OFFSETS, "width1" : 6 * mm, "oppositeDirection" : false, "width2" : 4 * mm, "tangentPropagation" : true});
        }
    });
